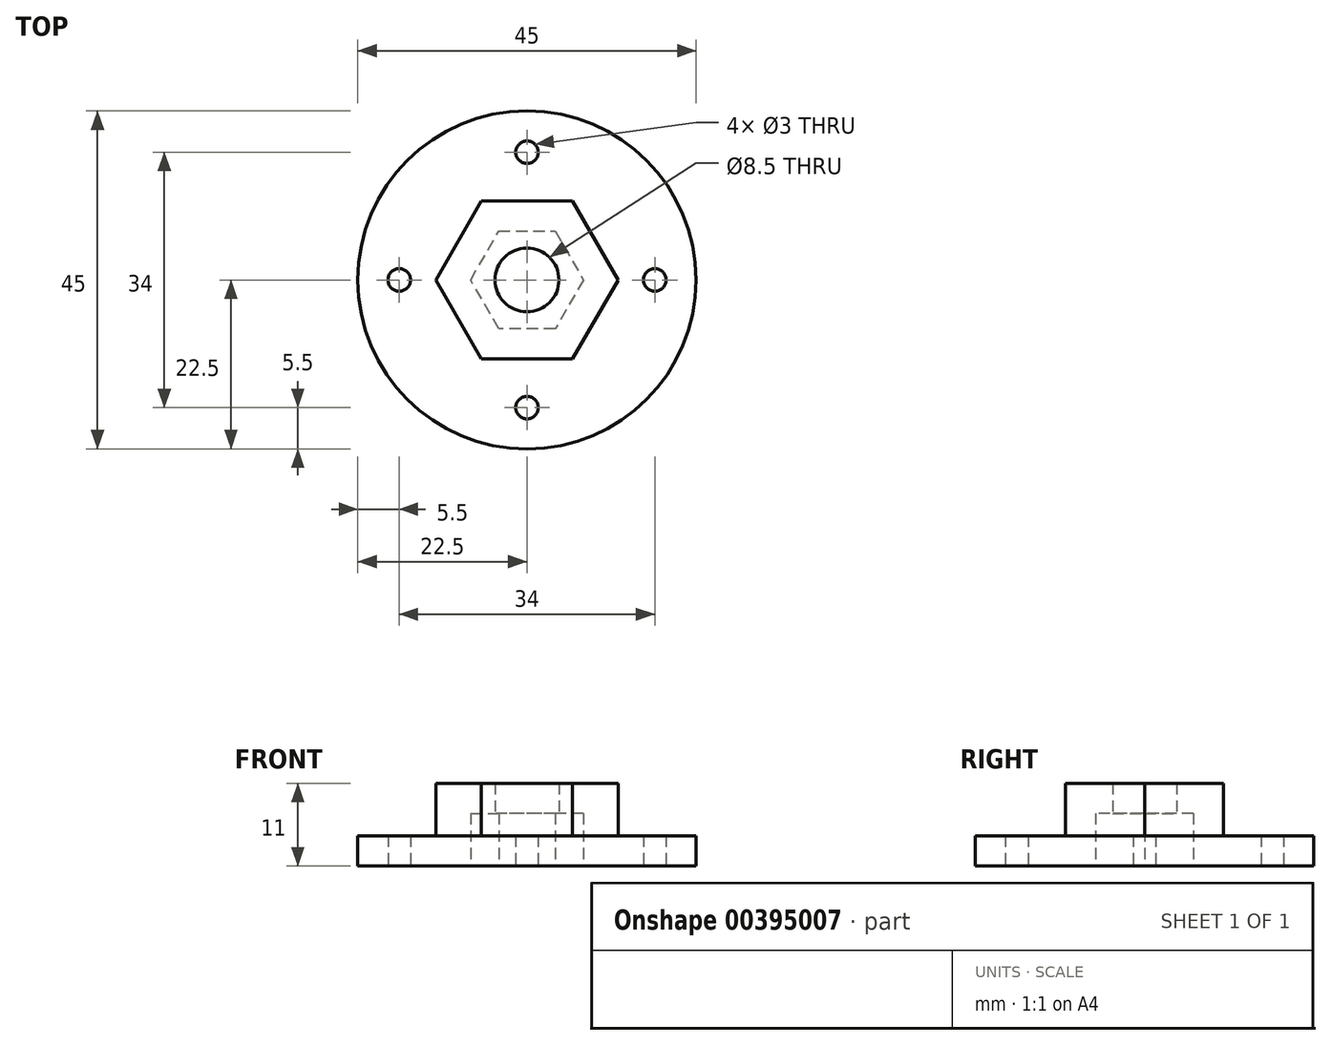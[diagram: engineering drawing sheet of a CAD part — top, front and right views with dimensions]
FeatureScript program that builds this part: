
annotation { "Feature Type Name" : "Feature", "Feature Type Description" : "" }
export const myFeature = defineFeature(function(context is Context, id is Id, definition is map)
    precondition{}
    {
        {
            var Q0;
            Q0=qCreatedBy(makeId("Top.planeOp"),FACE);
            var sketch = newSketch(context, id + "F0", { "sketchPlane" : qUnion([Q0])});
            skCircle(sketch, "E0.cCircle", {"center": v(0, 0) * mm, "radius": 6.5 * mm, "construction": true});
            skLineSegment(sketch, "E0.0", {"start": v(3.75, -6.5) * mm, "end": v(-3.75, -6.5) * mm});
            skLineSegment(sketch, "E0.1", {"start": v(-3.75, -6.5) * mm, "end": v(-7.5, 0) * mm});
            skLineSegment(sketch, "E0.2", {"start": v(-7.5, 0) * mm, "end": v(-3.75, 6.5) * mm});
            skLineSegment(sketch, "E0.3", {"start": v(-3.75, 6.5) * mm, "end": v(3.75, 6.5) * mm});
            skLineSegment(sketch, "E0.4", {"start": v(3.75, 6.5) * mm, "end": v(7.5, 0) * mm});
            skLineSegment(sketch, "E0.5", {"start": v(7.5, 0) * mm, "end": v(3.75, -6.5) * mm});
            skPoint(sketch, "E0.0.midPoint", {"position": v(0, -6.5) * mm});
            skCircle(sketch, "E1", {"center": v(0, 0) * mm, "radius": 22.5 * mm});
            skLineSegment(sketch, "E2.0", {"start": v(-6.06, -10.5) * mm, "end": v(-12.12, 0) * mm});
            skLineSegment(sketch, "E2.1", {"start": v(-6.06, 10.5) * mm, "end": v(6.06, 10.5) * mm});
            skLineSegment(sketch, "E2.2", {"start": v(6.06, 10.5) * mm, "end": v(12.12, 0) * mm});
            skLineSegment(sketch, "E2.3", {"start": v(-12.12, 0) * mm, "end": v(-6.06, 10.5) * mm});
            skLineSegment(sketch, "E2.4", {"start": v(12.12, 0) * mm, "end": v(6.06, -10.5) * mm});
            skLineSegment(sketch, "E2.5", {"start": v(6.06, -10.5) * mm, "end": v(-6.06, -10.5) * mm});
            skLineSegment(sketch, "E3", {"start": v(0, 0) * mm, "end": v(-17, 0) * mm, "construction": true});
            skCircle(sketch, "E4", {"center": v(-17, 0) * mm, "radius": 1.5 * mm});
            skCircle(sketch, "E5", {"center": v(-17, 0) * mm, "radius": 3.75 * mm});
            skCircle(sketch, "E6.MirrorC", {"center": v(17, 0) * mm, "radius": 1.5 * mm});
            skLineSegment(sketch, "E7", {"start": v(0, 0) * mm, "end": v(0, -17) * mm, "construction": true});
            skPoint(sketch, "E7.endSnap0", {"position": v(0, -10.5) * mm});
            skCircle(sketch, "E8", {"center": v(0, -17) * mm, "radius": 1.5 * mm});
            skCircle(sketch, "E9.MirrorC", {"center": v(0, 17) * mm, "radius": 1.5 * mm});
            skCircle(sketch, "E10", {"center": v(0, 0) * mm, "radius": 4.25 * mm});
            skSolve(sketch);
        }
        {
            var Q0;
            Q0=makeQuery(id+"F0.imprint","IMPRINT",FACE,{"disambiguationData":[TD([[makeQuery(id+"F0.imprint","IMPRINT",EDGE,{"derivedFrom":sQuery(id+"F0.wireOp",EDGE,"E1")}),1.0]])]});
            var Q1;
            Q1=makeQuery(id+"F0.imprint","IMPRINT",FACE,{"disambiguationData":[TD([[makeQuery(id+"F0.imprint","IMPRINT",EDGE,{"derivedFrom":sQuery(id+"F0.wireOp",EDGE,"E4")}),-1.0]])]});
            extrude(context, id + "F1", {"entities" : qUnion([Q0, Q1]), "depth" : 4 * mm});
        }
        {
            var Q0;
            Q0=makeQuery(id+"F0.imprint","IMPRINT",FACE,{"disambiguationData":[TD([[makeQuery(id+"F0.imprint","IMPRINT",EDGE,{"derivedFrom":sQuery(id+"F0.wireOp",EDGE,"E0.0")}),1.0]])]});
            var Q1;
            Q1=makeQuery(id+"F0.imprint","IMPRINT",FACE,{"disambiguationData":[TD([[makeQuery(id+"F0.imprint","IMPRINT",EDGE,{"derivedFrom":sQuery(id+"F0.wireOp",EDGE,"E0.0")}),-1.0]])]});
            var Q2;
            Q2=makeQuery(id+"F0.imprint","IMPRINT",FACE,{"disambiguationData":[TD([[makeQuery(id+"F0.imprint","IMPRINT",EDGE,{"derivedFrom":sQuery(id+"F0.wireOp",EDGE,"E10")}),1.0]])]});
            extrude(context, id + "F2", {"entities" : qUnion([Q0, Q1, Q2]), "operationType" : NewBodyOperationType.ADD, "depth" : 11 * mm});
        }
        {
            var Q0;
            Q0=makeQuery(id+"F0.imprint","IMPRINT",FACE,{"disambiguationData":[TD([[makeQuery(id+"F0.imprint","IMPRINT",EDGE,{"derivedFrom":sQuery(id+"F0.wireOp",EDGE,"E10")}),1.0]])]});
            extrude(context, id + "F3", {"entities" : qUnion([Q0]), "operationType" : NewBodyOperationType.REMOVE, "depth" : 25 * mm});
        }
        {
            var Q0;
            Q0=makeQuery(id+"F0.imprint","IMPRINT",FACE,{"disambiguationData":[TD([[makeQuery(id+"F0.imprint","IMPRINT",EDGE,{"derivedFrom":sQuery(id+"F0.wireOp",EDGE,"E0.0")}),-1.0]])]});
            extrude(context, id + "F4", {"entities" : qUnion([Q0]), "operationType" : NewBodyOperationType.REMOVE, "depth" : 7 * mm});
        }
    });
